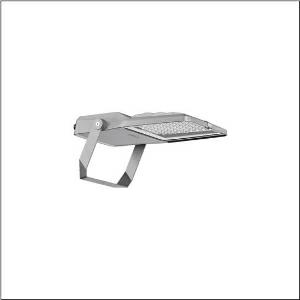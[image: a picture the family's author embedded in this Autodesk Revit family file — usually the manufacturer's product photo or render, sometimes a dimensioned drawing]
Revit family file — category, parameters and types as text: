
# Revit family: floodlight_fl_21_iq_mini___pl43_5xa7772c1a1a_56dc
name_source: partatom
category: Lighting Fixtures
units: mm (PartAtom-declared; Revit-internal decimal feet)

## family parameters
Cut with Voids When Loaded = No
Host = Face
Light Source = No
Part Type = Normal
Room Calculation Point = No
Round Connector Dimension = Use Diameter
Shared = No

## types (1)
- --- (1 x LED, 10370 lm, 87.2 W, 2200K)
    Apparent Load = 87 VA
    CIE Flux Codes = 27 78 99 100 100
    Color Rendering = 70
    Color Temperature = 2200K
    Default Elevation = 1800 mm
    Description = Floodlight FL 21 iQ mini, floodlight, primary light control with lens, of PMMA, primary optical cover: protective disc, of toughened safety glass, transparent, light distribution: PL43, light emission: direct distribution, installation type: surface-mounted, LED, High Power LED, rated luminous flux: 10.370lm, luminous efficacy: 119lm/W, light colour: 722, colour temperature: 2200K, control gear: iQ Street-Remote/DALI, control: Street-Remote, Auto-Match, Temp-Guard, Night-Set, Smart-Wire, Desk-Remote (wireless, voltage-free reading and setting of iQ features in the workshop via application-optimized NFC function/RFID function), optimised constant luminous flux control (CLO 2.0), with terminal, 6-pole, mains connection: 220..240V, AC, 50/60Hz, start of lifetime: 87W, end of service life: 92W, reduction: 40W, luminaire housing, of diecast aluminium, powder-coated, Siteco® metallic grey (DB 702S), corrosivity category C5 mid according to DIN EN ISO 12944, suitable for swimming pools, chlorine-resistant, sealing non-destructively replaceable, mounting bracket, of steel, galvanised, powder-coated, Siteco® metallic grey (DB 702S), protection rating (complete): IP66, insulation class (complete): insulation class II (safety insulation), certification: CE, ENEC, VDE, protection symbol: D, impact resistance: IK08, permissible operating ambient temperature: -40..+40°C, permissible operating ambient temperature for outdoor applications: -40..+50°C, standard: DIN EN 12944, LABS conformity tested according to VDMA 24364:2018-05, packaging unit: 1 piece

Light Distribution: PL43
    Height = 70 mm
    Lamp = 1 x LED
    Lamp Light Flux = 10370 lm
    Lamp Power = 87.2 W
    Lamp count = 1
    Length = 485 mm
    Luminous efficacy = 119 lm/W
    Manufacturer = Siteco
    ModVariant = No
    Model = 5XA7772C1A1A
    Number of Poles = 1
    OnlyDefault = Yes
    Power Factor = 1
    Product Name = Floodlight FL 21 iQ mini | PL43
    Product group = floodlight | pylon annexe
    ProductGroupID = 6200
    Protection Class = Protection class II
    Protection Degree = IP 66
    RLX_Detail_Level = 1
    RLX_Emergency_Light_Flux = 0 lm
    RLX_Emergency_Type = 0
    RLX_Emergency_Type_DB = No
    RlxData = <blob elided: 96181 chars, md5=7c14d68d>
    Socket = socket
    Standby Power = 0 W
    System Light Flux = 10370 lm
    System Power = 87 W
    Type Comments = factory setting: luminous flux: 100 % | dim-lin: 254 | 456 mA
    Type Image = l_1006845.jpg
    URL = http://relux.com
    VarID = @adj_162394
    Voltage = 0 V
    Weight = 0.00 kg
    Width = 337 mm

## geometry (parser evidence)
native form markers: Blend x4, Sweep x14
no freeform markers — native parametric forms only
